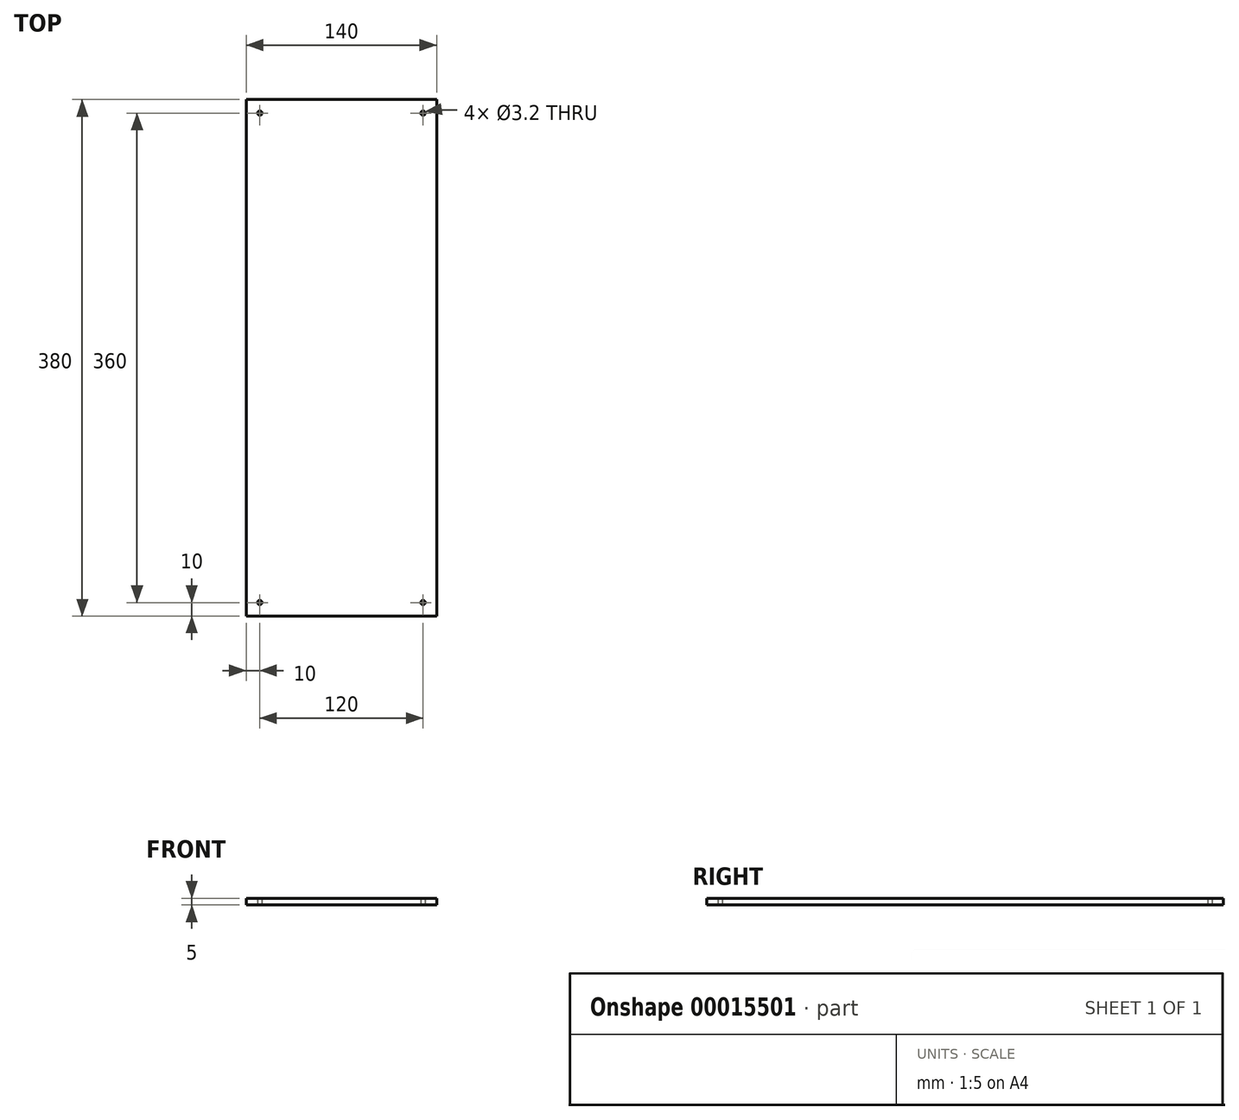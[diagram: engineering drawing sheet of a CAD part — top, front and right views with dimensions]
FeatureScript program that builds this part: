
annotation { "Feature Type Name" : "Feature", "Feature Type Description" : "" }
export const myFeature = defineFeature(function(context is Context, id is Id, definition is map)
    precondition{}
    {
        {
            var Q0;
            Q0=qCreatedBy(makeId("Top.planeOp"),FACE);
            var sketch = newSketch(context, id + "F0", { "sketchPlane" : qUnion([Q0])});
            skLineSegment(sketch, "E0.rect.bottom", {"start": v(-70, 190) * mm, "end": v(70, 190) * mm});
            skLineSegment(sketch, "E0.rect.top", {"start": v(-70, -190) * mm, "end": v(70, -190) * mm});
            skLineSegment(sketch, "E0.rect.left", {"start": v(-70, 190) * mm, "end": v(-70, -190) * mm});
            skLineSegment(sketch, "E0.rect.right", {"start": v(70, 190) * mm, "end": v(70, -190) * mm});
            skPoint(sketch, "E0.rect.middle", {"position": v(0, 0) * mm});
            skSolve(sketch);
        }
        {
            var Q0;
            Q0 = qSketchRegion(id + "F0", true);
            extrude(context, id + "F1", {"entities" : qUnion([Q0]), "depth" : 5 * mm});
        }
        {
            var Q0;
            Q0=qCreatedBy(makeId("Top.planeOp"),FACE);
            var sketch = newSketch(context, id + "F2", { "sketchPlane" : qUnion([Q0])});
            skLineSegment(sketch, "E1.rect.bottom", {"start": v(60, 180) * mm, "end": v(-60, 180) * mm, "construction": true});
            skLineSegment(sketch, "E1.rect.top", {"start": v(60, -180) * mm, "end": v(-60, -180) * mm, "construction": true});
            skLineSegment(sketch, "E1.rect.left", {"start": v(60, 180) * mm, "end": v(60, -180) * mm, "construction": true});
            skLineSegment(sketch, "E1.rect.right", {"start": v(-60, 180) * mm, "end": v(-60, -180) * mm, "construction": true});
            skPoint(sketch, "E1.rect.middle", {"position": v(0, 0) * mm});
            skPoint(sketch, "E2", {"position": v(-60, -180) * mm});
            skPoint(sketch, "E3", {"position": v(60, -180) * mm});
            skPoint(sketch, "E4", {"position": v(60, 180) * mm});
            skPoint(sketch, "E5", {"position": v(-60, 180) * mm});
            skSolve(sketch);
        }
        {
            var Q0;
            Q0=sQuery(id+"F2.wireOp",VERTEX,"E2");
            var Q1;
            Q1=sQuery(id+"F2.wireOp",VERTEX,"E3");
            var Q2;
            Q2=sQuery(id+"F2.wireOp",VERTEX,"E4");
            var Q3;
            Q3=sQuery(id+"F2.wireOp",VERTEX,"E5");
            var Q4;
            Q4=makeQuery(id+"F1.opExtrude","SWEPT_BODY",BODY,{"disambiguationData":[OSD([sQuery(id+"F0.wireOp",EDGE,"E0.rect.bottom"),sQuery(id+"F0.wireOp",EDGE,"E0.rect.top"),sQuery(id+"F0.wireOp",EDGE,"E0.rect.left"),sQuery(id+"F0.wireOp",EDGE,"E0.rect.right")])]});
            hole(context, id + "F3", {"style" : HoleStyle.SIMPLE, "holeDiameter" : 3.2 * mm, "endStyle" : HoleEndStyle.THROUGH, "oppositeDirection" : true, "locations" : qUnion([Q0, Q1, Q2, Q3]), "scope" : qUnion([Q4])});
        }
    });
